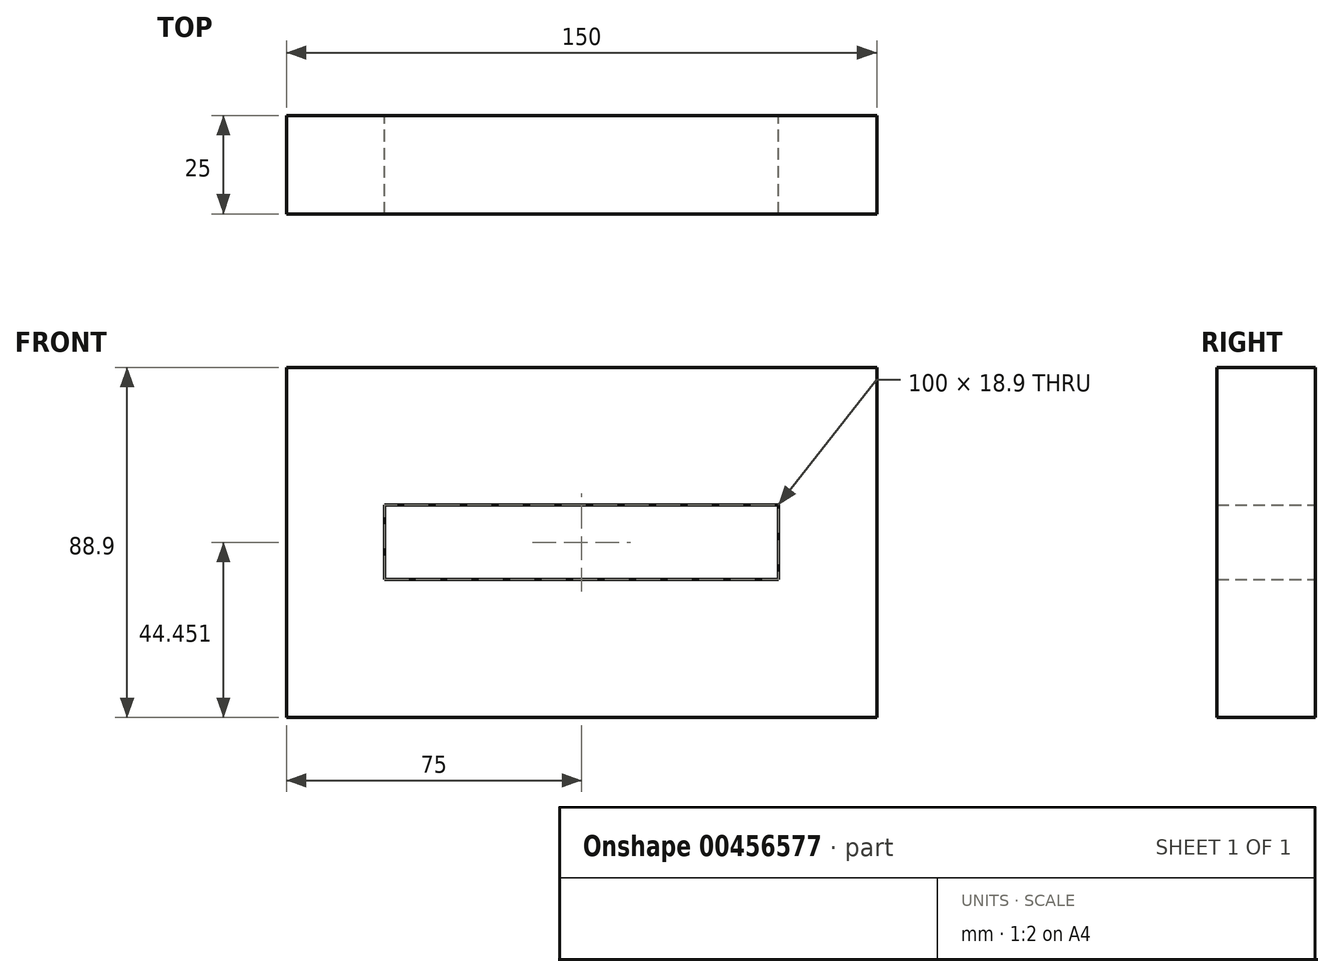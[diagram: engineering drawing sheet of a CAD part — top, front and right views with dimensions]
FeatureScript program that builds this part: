
annotation { "Feature Type Name" : "Feature", "Feature Type Description" : "" }
export const myFeature = defineFeature(function(context is Context, id is Id, definition is map)
    precondition{}
    {
        {
            var Q0;
            Q0=qCreatedBy(makeId("Front.planeOp"),FACE);
            var sketch = newSketch(context, id + "F0", { "sketchPlane" : qUnion([Q0])});
            skLineSegment(sketch, "E0.bottom", {"start": v(-71.87, 39.72) * mm, "end": v(78.13, 39.72) * mm});
            skLineSegment(sketch, "E0.top", {"start": v(-71.87, -49.18) * mm, "end": v(78.13, -49.18) * mm});
            skLineSegment(sketch, "E0.left", {"start": v(-71.87, 39.72) * mm, "end": v(-71.87, -49.18) * mm});
            skLineSegment(sketch, "E0.right", {"start": v(78.13, 39.72) * mm, "end": v(78.13, -49.18) * mm});
            skLineSegment(sketch, "E1.bottom", {"start": v(-46.87, 4.72) * mm, "end": v(53.13, 4.72) * mm});
            skLineSegment(sketch, "E1.top", {"start": v(-46.87, -14.18) * mm, "end": v(53.13, -14.18) * mm});
            skLineSegment(sketch, "E1.left", {"start": v(-46.87, 4.72) * mm, "end": v(-46.87, -14.18) * mm});
            skLineSegment(sketch, "E1.right", {"start": v(53.13, 4.72) * mm, "end": v(53.13, -14.18) * mm});
            skSolve(sketch);
        }
        {
            var Q0;
            Q0=makeQuery(id+"F0.imprint","IMPRINT",FACE,{"disambiguationData":[TD([[makeQuery(id+"F0.imprint","IMPRINT",EDGE,{"derivedFrom":sQuery(id+"F0.wireOp",EDGE,"E0.bottom")}),-1.0]])]});
            extrude(context, id + "F1", {"entities" : qUnion([Q0]), "depth" : 25 * mm});
        }
        {
            var Q0;
            Q0=makeQuery(id+"F0.imprint","IMPRINT",FACE,{"disambiguationData":[TD([[makeQuery(id+"F0.imprint","IMPRINT",EDGE,{"derivedFrom":sQuery(id+"F0.wireOp",EDGE,"E1.bottom")}),-1.0]])]});
            extrude(context, id + "F2", {"entities" : qUnion([Q0]), "operationType" : NewBodyOperationType.REMOVE, "endBound" : BoundingType.THROUGH_ALL, "oppositeDirection" : true, "depth" : 50 * mm});
        }
    });
